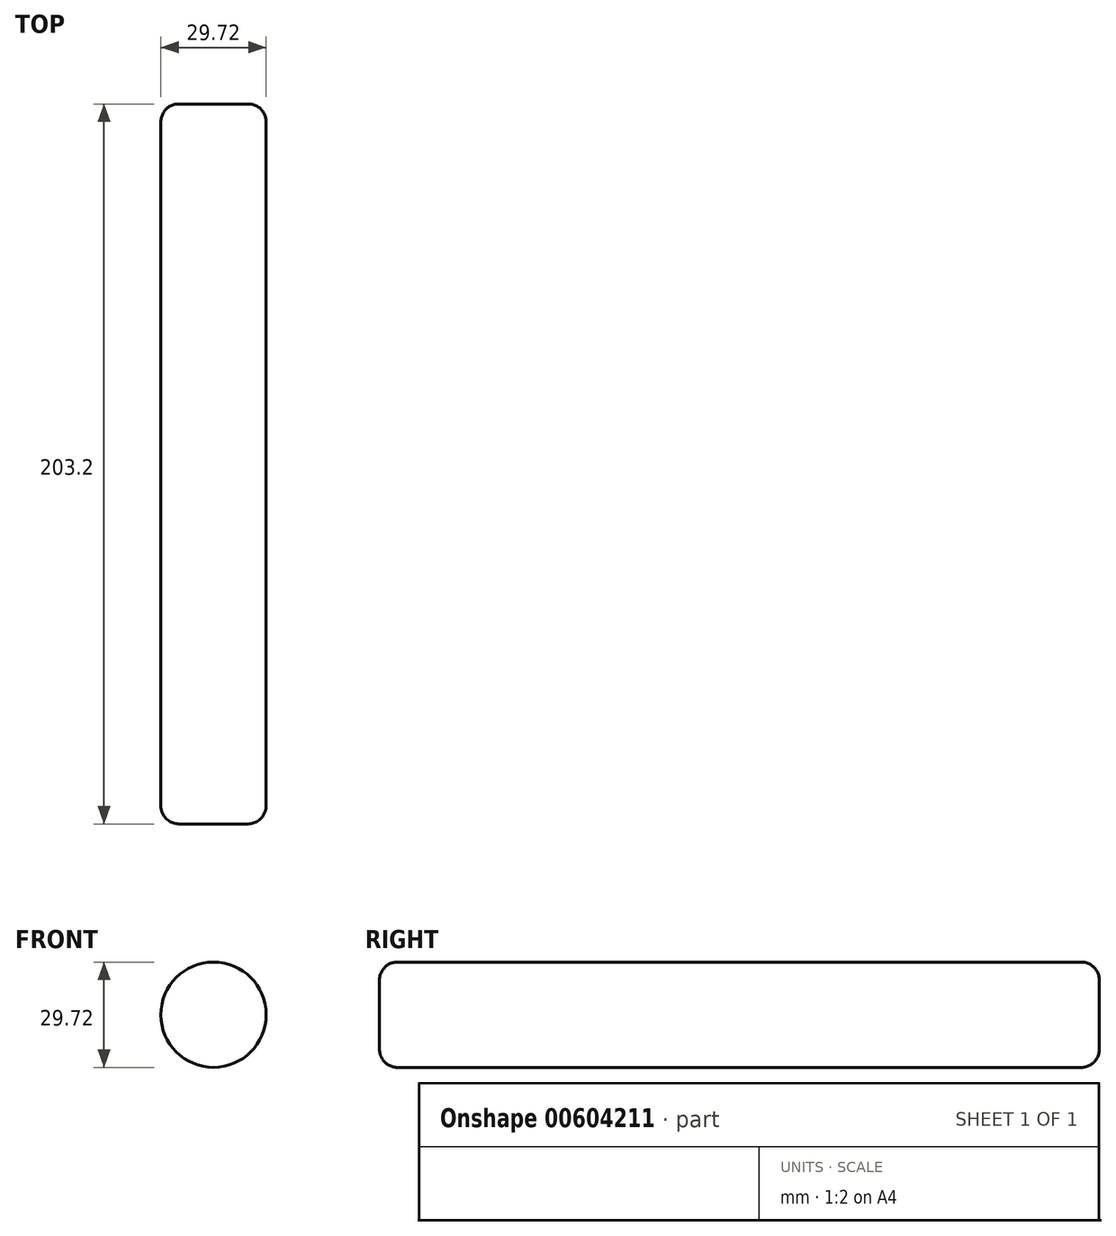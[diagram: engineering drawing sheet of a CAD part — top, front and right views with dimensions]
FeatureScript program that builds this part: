
annotation { "Feature Type Name" : "Feature", "Feature Type Description" : "" }
export const myFeature = defineFeature(function(context is Context, id is Id, definition is map)
    precondition{}
    {
        {
            var Q0;
            Q0=qCreatedBy(makeId("Front.planeOp"),FACE);
            var sketch = newSketch(context, id + "F0", { "sketchPlane" : qUnion([Q0])});
            skCircle(sketch, "E0", {"center": v(0, 0) * mm, "radius": 14.86 * mm});
            skSolve(sketch);
        }
        {
            var Q0;
            Q0=makeQuery(id+"F0.imprint","IMPRINT",FACE,{"disambiguationData":[TD([[makeQuery(id+"F0.imprint","IMPRINT",EDGE,{"derivedFrom":sQuery(id+"F0.wireOp",EDGE,"E0")}),1.0]])]});
            extrude(context, id + "F1", {"entities" : qUnion([Q0]), "depth" : 203.2 * mm, "offsetDistance" : 25.4 * mm});
        }
        {
            var Q0;
            Q0=makeQuery(id+"F1.opExtrude","SWEPT_FACE",FACE,{"disambiguationData":[OSD([sQuery(id+"F0.wireOp",EDGE,"E0")])]});
            fillet(context, id + "F2", {"entities" : qUnion([Q0]), "radius" : 5.08 * mm, "tangentPropagation" : true, "allowEdgeOverflow" : false});
        }
        {
            var Q0;
            Q0=qCreatedBy(makeId("Right.planeOp"),FACE);
            var sketch = newSketch(context, id + "F3", { "sketchPlane" : qUnion([Q0])});
            skCircle(sketch, "E1", {"center": v(-178.63, 0) * mm, "radius": 11.08 * mm});
            skCircle(sketch, "E2", {"center": v(-141.45, 0) * mm, "radius": 11.32 * mm});
            skCircle(sketch, "E3", {"center": v(-108.02, 0) * mm, "radius": 11.66 * mm});
            skCircle(sketch, "E4", {"center": v(-75.61, 0) * mm, "radius": 11.41 * mm});
            skCircle(sketch, "E5", {"center": v(-42.86, 0) * mm, "radius": 11.41 * mm});
            skSolve(sketch);
        }
        {
            var Q0;
            Q0 = qSketchRegion(id + "F3", true);
            extrude(context, id + "F4", {"entities" : qUnion([Q0]), "operationType" : NewBodyOperationType.ADD, "endBound" : BoundingType.UP_TO_NEXT, "oppositeDirection" : true, "depth" : 25.4 * mm, "offsetDistance" : 25.4 * mm});
        }
    });
